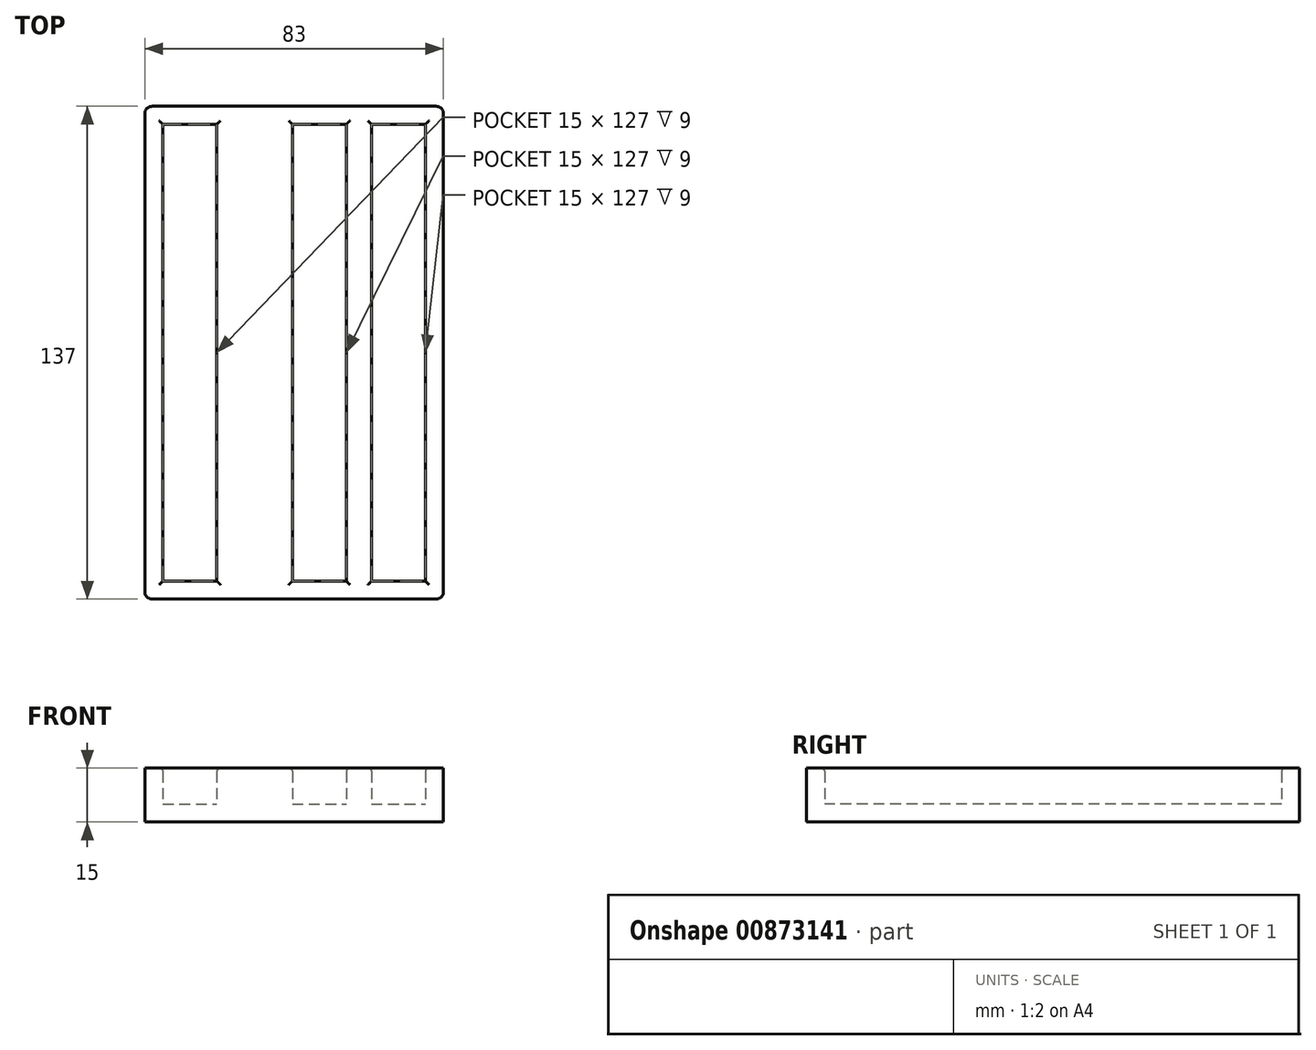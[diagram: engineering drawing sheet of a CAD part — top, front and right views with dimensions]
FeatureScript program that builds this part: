
annotation { "Feature Type Name" : "Feature", "Feature Type Description" : "" }
export const myFeature = defineFeature(function(context is Context, id is Id, definition is map)
    precondition{}
    {
        {
            var Q0;
            Q0=qCreatedBy(makeId("Top.planeOp"),FACE);
            var sketch = newSketch(context, id + "F0", { "sketchPlane" : qUnion([Q0])});
            skLineSegment(sketch, "E0.bottom", {"start": v(-36.5, 63.5) * mm, "end": v(-21.5, 63.5) * mm});
            skLineSegment(sketch, "E0.top", {"start": v(-36.5, -63.5) * mm, "end": v(-21.5, -63.5) * mm});
            skLineSegment(sketch, "E0.left", {"start": v(-36.5, 63.5) * mm, "end": v(-36.5, -63.5) * mm});
            skLineSegment(sketch, "E0.right", {"start": v(-21.5, 63.5) * mm, "end": v(-21.5, -63.5) * mm});
            skLineSegment(sketch, "E1.bottom", {"start": v(21.5, 63.5) * mm, "end": v(36.5, 63.5) * mm});
            skLineSegment(sketch, "E1.top", {"start": v(21.5, -63.5) * mm, "end": v(36.5, -63.5) * mm});
            skLineSegment(sketch, "E1.left", {"start": v(21.5, 63.5) * mm, "end": v(21.5, -63.5) * mm});
            skLineSegment(sketch, "E1.right", {"start": v(36.5, 63.5) * mm, "end": v(36.5, -63.5) * mm});
            skLineSegment(sketch, "E2.bottom", {"start": v(-0.5, 63.5) * mm, "end": v(14.5, 63.5) * mm});
            skLineSegment(sketch, "E2.top", {"start": v(-0.5, -63.5) * mm, "end": v(14.5, -63.5) * mm});
            skLineSegment(sketch, "E2.left", {"start": v(-0.5, 63.5) * mm, "end": v(-0.5, -63.5) * mm});
            skLineSegment(sketch, "E2.right", {"start": v(14.5, 63.5) * mm, "end": v(14.5, -63.5) * mm});
            skSolve(sketch);
        }
        {
            var Q0;
            Q0=qCreatedBy(makeId("Top.planeOp"),FACE);
            var sketch = newSketch(context, id + "F1", { "sketchPlane" : qUnion([Q0])});
            skLineSegment(sketch, "E3.bottom", {"start": v(-41.5, 68.5) * mm, "end": v(41.5, 68.5) * mm});
            skLineSegment(sketch, "E3.top", {"start": v(-41.5, -68.5) * mm, "end": v(41.5, -68.5) * mm});
            skLineSegment(sketch, "E3.left", {"start": v(-41.5, 68.5) * mm, "end": v(-41.5, -68.5) * mm});
            skLineSegment(sketch, "E3.right", {"start": v(41.5, 68.5) * mm, "end": v(41.5, -68.5) * mm});
            skSolve(sketch);
        }
        {
            var Q0;
            Q0 = qSketchRegion(id + "F1", true);
            extrude(context, id + "F2", {"entities" : qUnion([Q0]), "endBound" : BoundingType.SYMMETRIC, "depth" : 10 * mm, "offsetDistance" : 25 * mm});
        }
        {
            var Q0;
            Q0 = qSketchRegion(id + "F0", true);
            extrude(context, id + "F3", {"entities" : qUnion([Q0]), "operationType" : NewBodyOperationType.REMOVE, "depth" : 25 * mm, "offsetDistance" : 25 * mm});
        }
        {
            var Q0;
            Q0=makeQuery(id+"F2.opExtrude","SWEPT_EDGE",EDGE,{"disambiguationData":[OSD([sQuery(id+"F1.wireOp",EDGE,"E3.top"),sQuery(id+"F1.wireOp",EDGE,"E3.left")])]});
            var Q1;
            Q1=makeQuery(id+"F2.opExtrude","SWEPT_EDGE",EDGE,{"disambiguationData":[OSD([sQuery(id+"F1.wireOp",EDGE,"E3.top"),sQuery(id+"F1.wireOp",EDGE,"E3.right")])]});
            var Q2;
            Q2=makeQuery(id+"F2.opExtrude","SWEPT_EDGE",EDGE,{"disambiguationData":[OSD([sQuery(id+"F1.wireOp",EDGE,"E3.bottom"),sQuery(id+"F1.wireOp",EDGE,"E3.right")])]});
            var Q3;
            Q3=makeQuery(id+"F2.opExtrude","SWEPT_EDGE",EDGE,{"disambiguationData":[OSD([sQuery(id+"F1.wireOp",EDGE,"E3.bottom"),sQuery(id+"F1.wireOp",EDGE,"E3.left")])]});
            fillet(context, id + "F4", {"entities" : qUnion([Q0, Q1, Q2, Q3]), "radius" : 2 * mm, "tangentPropagation" : true, "allowEdgeOverflow" : false});
        }
        {
            var Q0;
            Q0=makeQuery(id+"F2.opExtrude","CAP_FACE",FACE,{"disambiguationData":[OSD([sQuery(id+"F1.wireOp",EDGE,"E3.bottom"),sQuery(id+"F1.wireOp",EDGE,"E3.top"),sQuery(id+"F1.wireOp",EDGE,"E3.left"),sQuery(id+"F1.wireOp",EDGE,"E3.right")])],"isStart":false});
            extrude(context, id + "F5", {"entities" : qUnion([Q0]), "operationType" : NewBodyOperationType.ADD, "depth" : 5 * mm, "offsetDistance" : 25 * mm});
        }
        {
            var Q0;
            Q0=makeQuery(id+"F5.opExtrude","CAP_EDGE",EDGE,{"disambiguationData":[OSD([sQuery(id+"F0.wireOp",EDGE,"E0.right"),sQuery(id+"F1.wireOp",EDGE,"E3.bottom"),sQuery(id+"F1.wireOp",EDGE,"E3.top"),sQuery(id+"F1.wireOp",EDGE,"E3.left"),sQuery(id+"F1.wireOp",EDGE,"E3.right")])],"isStart":false});
            var Q1;
            Q1=makeQuery(id+"F5.opExtrude","CAP_EDGE",EDGE,{"disambiguationData":[OSD([sQuery(id+"F0.wireOp",EDGE,"E0.bottom"),sQuery(id+"F1.wireOp",EDGE,"E3.bottom"),sQuery(id+"F1.wireOp",EDGE,"E3.top"),sQuery(id+"F1.wireOp",EDGE,"E3.left"),sQuery(id+"F1.wireOp",EDGE,"E3.right")])],"isStart":false});
            var Q2;
            Q2=makeQuery(id+"F5.opExtrude","CAP_EDGE",EDGE,{"disambiguationData":[OSD([sQuery(id+"F0.wireOp",EDGE,"E0.left"),sQuery(id+"F1.wireOp",EDGE,"E3.bottom"),sQuery(id+"F1.wireOp",EDGE,"E3.top"),sQuery(id+"F1.wireOp",EDGE,"E3.left"),sQuery(id+"F1.wireOp",EDGE,"E3.right")])],"isStart":false});
            var Q3;
            Q3=makeQuery(id+"F5.opExtrude","CAP_EDGE",EDGE,{"disambiguationData":[OSD([sQuery(id+"F0.wireOp",EDGE,"E0.top"),sQuery(id+"F1.wireOp",EDGE,"E3.bottom"),sQuery(id+"F1.wireOp",EDGE,"E3.top"),sQuery(id+"F1.wireOp",EDGE,"E3.left"),sQuery(id+"F1.wireOp",EDGE,"E3.right")])],"isStart":false});
            var Q4;
            Q4=makeQuery(id+"F5.opExtrude","CAP_EDGE",EDGE,{"disambiguationData":[OSD([sQuery(id+"F0.wireOp",EDGE,"E2.left"),sQuery(id+"F1.wireOp",EDGE,"E3.bottom"),sQuery(id+"F1.wireOp",EDGE,"E3.top"),sQuery(id+"F1.wireOp",EDGE,"E3.left"),sQuery(id+"F1.wireOp",EDGE,"E3.right")])],"isStart":false});
            var Q5;
            Q5=makeQuery(id+"F5.opExtrude","CAP_EDGE",EDGE,{"disambiguationData":[OSD([sQuery(id+"F0.wireOp",EDGE,"E2.right"),sQuery(id+"F1.wireOp",EDGE,"E3.bottom"),sQuery(id+"F1.wireOp",EDGE,"E3.top"),sQuery(id+"F1.wireOp",EDGE,"E3.left"),sQuery(id+"F1.wireOp",EDGE,"E3.right")])],"isStart":false});
            var Q6;
            Q6=makeQuery(id+"F5.opExtrude","CAP_EDGE",EDGE,{"disambiguationData":[OSD([sQuery(id+"F0.wireOp",EDGE,"E2.bottom"),sQuery(id+"F1.wireOp",EDGE,"E3.bottom"),sQuery(id+"F1.wireOp",EDGE,"E3.top"),sQuery(id+"F1.wireOp",EDGE,"E3.left"),sQuery(id+"F1.wireOp",EDGE,"E3.right")])],"isStart":false});
            var Q7;
            Q7=makeQuery(id+"F5.opExtrude","CAP_EDGE",EDGE,{"disambiguationData":[OSD([sQuery(id+"F0.wireOp",EDGE,"E2.top"),sQuery(id+"F1.wireOp",EDGE,"E3.bottom"),sQuery(id+"F1.wireOp",EDGE,"E3.top"),sQuery(id+"F1.wireOp",EDGE,"E3.left"),sQuery(id+"F1.wireOp",EDGE,"E3.right")])],"isStart":false});
            var Q8;
            Q8=makeQuery(id+"F5.opExtrude","CAP_EDGE",EDGE,{"disambiguationData":[OSD([sQuery(id+"F0.wireOp",EDGE,"E1.bottom"),sQuery(id+"F1.wireOp",EDGE,"E3.bottom"),sQuery(id+"F1.wireOp",EDGE,"E3.top"),sQuery(id+"F1.wireOp",EDGE,"E3.left"),sQuery(id+"F1.wireOp",EDGE,"E3.right")])],"isStart":false});
            var Q9;
            Q9=makeQuery(id+"F5.opExtrude","CAP_EDGE",EDGE,{"disambiguationData":[OSD([sQuery(id+"F0.wireOp",EDGE,"E1.left"),sQuery(id+"F1.wireOp",EDGE,"E3.bottom"),sQuery(id+"F1.wireOp",EDGE,"E3.top"),sQuery(id+"F1.wireOp",EDGE,"E3.left"),sQuery(id+"F1.wireOp",EDGE,"E3.right")])],"isStart":false});
            var Q10;
            Q10=makeQuery(id+"F5.opExtrude","CAP_EDGE",EDGE,{"disambiguationData":[OSD([sQuery(id+"F0.wireOp",EDGE,"E1.right"),sQuery(id+"F1.wireOp",EDGE,"E3.bottom"),sQuery(id+"F1.wireOp",EDGE,"E3.top"),sQuery(id+"F1.wireOp",EDGE,"E3.left"),sQuery(id+"F1.wireOp",EDGE,"E3.right")])],"isStart":false});
            var Q11;
            Q11=makeQuery(id+"F5.opExtrude","CAP_EDGE",EDGE,{"disambiguationData":[OSD([sQuery(id+"F0.wireOp",EDGE,"E1.top"),sQuery(id+"F1.wireOp",EDGE,"E3.bottom"),sQuery(id+"F1.wireOp",EDGE,"E3.top"),sQuery(id+"F1.wireOp",EDGE,"E3.left"),sQuery(id+"F1.wireOp",EDGE,"E3.right")])],"isStart":false});
            fillet(context, id + "F6", {"entities" : qUnion([Q0, Q1, Q2, Q3, Q4, Q5, Q6, Q7, Q8, Q9, Q10, Q11]), "radius" : 1 * mm, "tangentPropagation" : true, "allowEdgeOverflow" : false});
        }
    });
